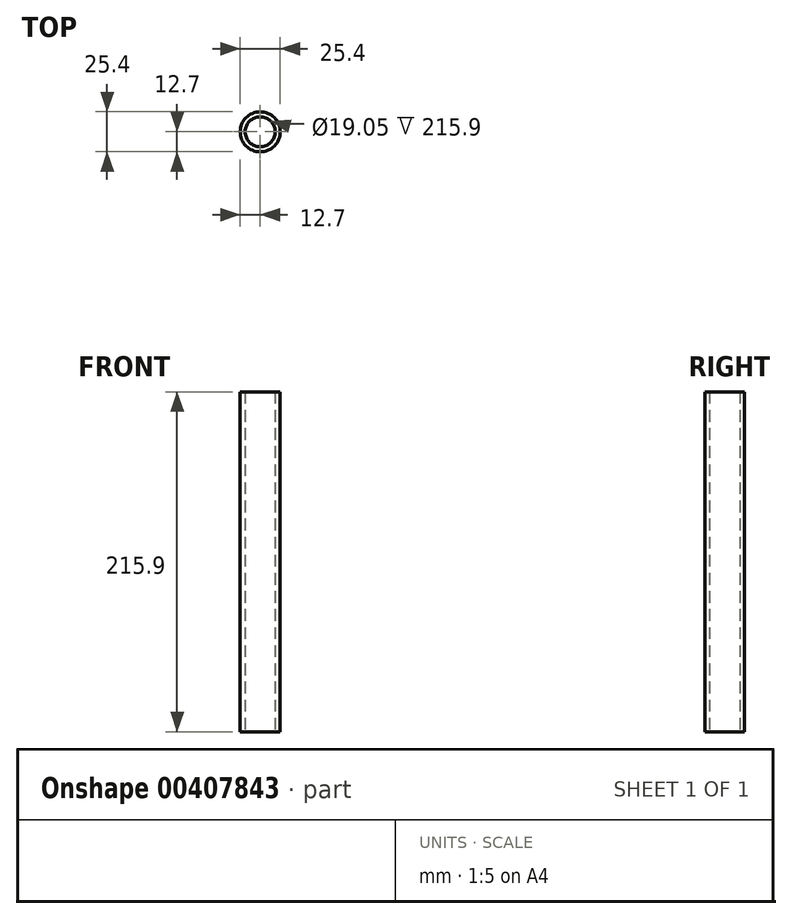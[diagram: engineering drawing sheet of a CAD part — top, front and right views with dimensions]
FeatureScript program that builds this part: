
annotation { "Feature Type Name" : "Feature", "Feature Type Description" : "" }
export const myFeature = defineFeature(function(context is Context, id is Id, definition is map)
    precondition{}
    {
        {
            var Q0;
            Q0=qCreatedBy(makeId("Top.planeOp"),FACE);
            var sketch = newSketch(context, id + "F0", { "sketchPlane" : qUnion([Q0])});
            skCircle(sketch, "E0", {"center": v(0, 0) * mm, "radius": 9.53 * mm});
            skCircle(sketch, "E1", {"center": v(0, 0) * mm, "radius": 12.7 * mm});
            skSolve(sketch);
        }
        {
            var Q0;
            Q0=makeQuery(id+"F0.imprint","IMPRINT",FACE,{"disambiguationData":[TD([[makeQuery(id+"F0.imprint","IMPRINT",EDGE,{"derivedFrom":sQuery(id+"F0.wireOp",EDGE,"E0")}),-1.0]])]});
            extrude(context, id + "F1", {"entities" : qUnion([Q0]), "endBound" : BoundingType.SYMMETRIC, "depth" : 215.9 * mm});
        }
    });
